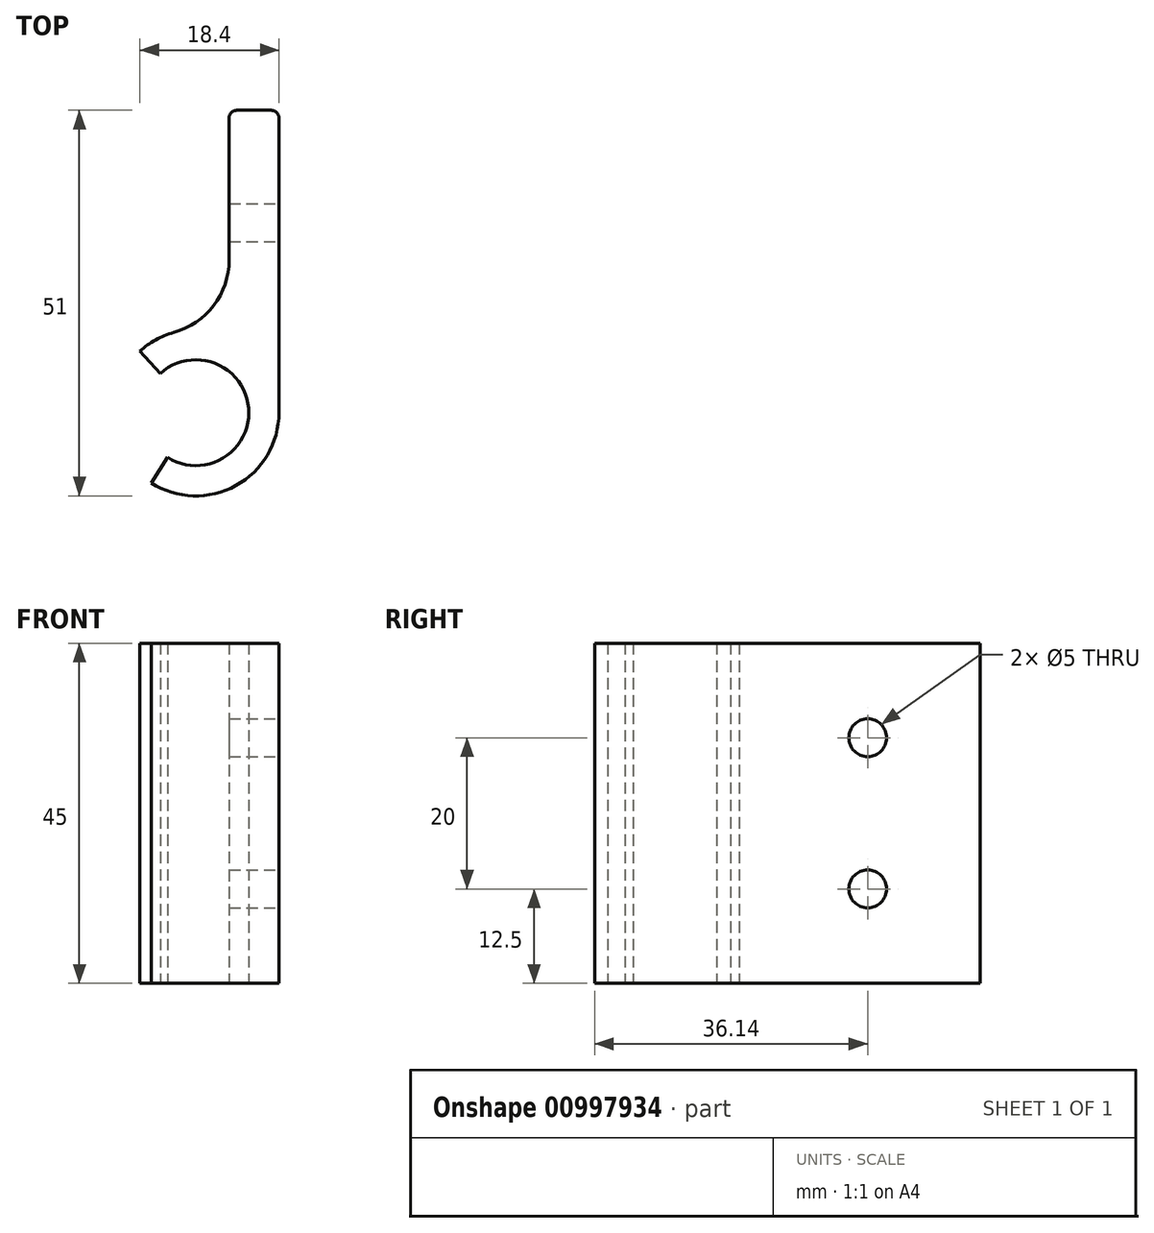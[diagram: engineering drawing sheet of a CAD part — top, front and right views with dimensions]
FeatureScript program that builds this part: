
annotation { "Feature Type Name" : "Feature", "Feature Type Description" : "" }
export const myFeature = defineFeature(function(context is Context, id is Id, definition is map)
    precondition{}
    {
        {
            var Q0;
            Q0=qCreatedBy(makeId("Top.planeOp"),FACE);
            var sketch = newSketch(context, id + "F0", { "sketchPlane" : qUnion([Q0])});
            skArc(sketch, "E0", {"start": v(-3.76, -5.9) * mm, "mid": v(6.97, 0.6) * mm, "end": v(-4.7, 5.18) * mm});
            skArc(sketch, "E1", {"start": v(-2.93, 10.6) * mm, "mid": v(-5.31, 9.63) * mm, "end": v(-7.4, 8.14) * mm});
            skLineSegment(sketch, "E2", {"start": v(11, 0) * mm, "end": v(11, 39) * mm});
            skLineSegment(sketch, "E3", {"start": v(10, 40) * mm, "end": v(5.4, 40) * mm});
            skLineSegment(sketch, "E4.trimOffspring", {"start": v(4.4, 20.24) * mm, "end": v(4.4, 39) * mm});
            skLineSegment(sketch, "E5", {"start": v(0, 11) * mm, "end": v(-10, 11) * mm, "construction": true});
            skLineSegment(sketch, "E6", {"start": v(0, -11) * mm, "end": v(-7, -11) * mm, "construction": true});
            skLineSegment(sketch, "E7", {"start": v(0, 0) * mm, "end": v(-7, -11) * mm, "construction": true});
            skLineSegment(sketch, "E8", {"start": v(0, 0) * mm, "end": v(-10, 11) * mm, "construction": true});
            skArc(sketch, "E9.trimOffspring", {"start": v(-5.9, -9.28) * mm, "mid": v(5.3, -9.64) * mm, "end": v(11, 0) * mm});
            skPoint(sketch, "E10.visualSharp", {"position": v(4.4, 10.08) * mm});
            skArc(sketch, "E10.filletArc", {"start": v(-2.93, 10.6) * mm, "mid": v(2.36, 14.18) * mm, "end": v(4.4, 20.24) * mm});
            skPoint(sketch, "E11.visualSharp", {"position": v(4.4, 40) * mm});
            skArc(sketch, "E11.filletArc", {"start": v(5.4, 40) * mm, "mid": v(4.7, 39.7) * mm, "end": v(4.4, 39) * mm});
            skPoint(sketch, "E12.visualSharp", {"position": v(11, 40) * mm});
            skArc(sketch, "E12.filletArc", {"start": v(11, 39) * mm, "mid": v(10.7, 39.7) * mm, "end": v(10, 40) * mm});
            skLineSegment(sketch, "E13", {"start": v(-7.4, 8.14) * mm, "end": v(-4.7, 5.18) * mm});
            skLineSegment(sketch, "E14", {"start": v(-5.9, -9.28) * mm, "end": v(-3.76, -5.9) * mm});
            skSolve(sketch);
        }
        {
            var Q0;
            Q0=makeQuery(id+"F0.imprint","IMPRINT",FACE,{"disambiguationData":[TD([[makeQuery(id+"F0.imprint","IMPRINT",EDGE,{"derivedFrom":sQuery(id+"F0.wireOp",EDGE,"E0")}),-1.0]])]});
            extrude(context, id + "F1", {"entities" : qUnion([Q0]), "depth" : 45 * mm, "offsetDistance" : 25 * mm});
        }
        {
            var Q0;
            Q0=qCreatedBy(makeId("Top.planeOp"),FACE);
            var sketch = newSketch(context, id + "F2", { "sketchPlane" : qUnion([Q0])});
            skLineSegment(sketch, "E15", {"start": v(0, 0) * mm, "end": v(0, 25) * mm});
            skLineSegment(sketch, "E16", {"start": v(0, 25) * mm, "end": v(10.62, 25) * mm});
            skLineSegment(sketch, "E17.0.0", {"start": v(4.4, 39) * mm, "end": v(4.4, 20.24) * mm});
            skLineSegment(sketch, "E17.0.2", {"start": v(4.4, 20.24) * mm, "end": v(4.4, 39) * mm});
            skSolve(sketch);
        }
        {
            var Q0;
            Q0=makeQuery(id+"F1.opExtrude","SWEPT_FACE",FACE,{"disambiguationData":[OSD([sQuery(id+"F0.wireOp",EDGE,"E2")])]});
            var sketch = newSketch(context, id + "F3", { "sketchPlane" : qUnion([Q0])});
            skLineSegment(sketch, "E18", {"start": v(25.14, 0) * mm, "end": v(25.14, 45) * mm, "construction": true});
            skLineSegment(sketch, "E19.0", {"start": v(39, 12.5) * mm, "end": v(19.08, 12.5) * mm, "construction": true});
            skLineSegment(sketch, "E20.0", {"start": v(39, 32.5) * mm, "end": v(19.08, 32.5) * mm, "construction": true});
            skCircle(sketch, "E21", {"center": v(25.14, 32.5) * mm, "radius": 2.5 * mm});
            skCircle(sketch, "E22", {"center": v(25.14, 12.5) * mm, "radius": 2.5 * mm});
            skSolve(sketch);
        }
        {
            var Q0;
            Q0=makeQuery(id+"F3.imprint","IMPRINT",FACE,{"disambiguationData":[TD([[makeQuery(id+"F3.imprint","IMPRINT",EDGE,{"derivedFrom":sQuery(id+"F3.wireOp",EDGE,"E21")}),1.0]])]});
            var Q1;
            Q1=makeQuery(id+"F3.imprint","IMPRINT",FACE,{"disambiguationData":[TD([[makeQuery(id+"F3.imprint","IMPRINT",EDGE,{"derivedFrom":sQuery(id+"F3.wireOp",EDGE,"E22")}),1.0]])]});
            extrude(context, id + "F4", {"entities" : qUnion([Q0, Q1]), "operationType" : NewBodyOperationType.REMOVE, "endBound" : BoundingType.THROUGH_ALL, "oppositeDirection" : true, "depth" : 6 * mm, "offsetDistance" : 25 * mm});
        }
    });
